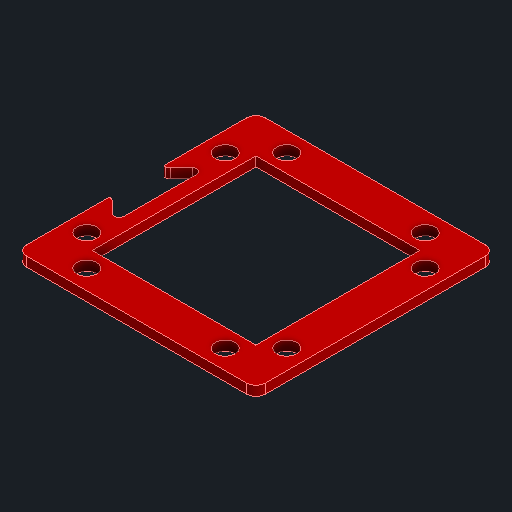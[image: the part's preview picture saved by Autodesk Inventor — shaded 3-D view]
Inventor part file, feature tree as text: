
AUTODESK INVENTOR PART (.ipt)
format: ipt  version: 2023.4 (Build 274418000, 418)  size: 366,080 bytes
history: native  units: mm
features: reference x9, extrude x3, other x3, sketch x2, fillet x1, projected_geometry x1
ambient origin geometry x8: Origin, YZ Plane, XZ Plane, XY Plane, X Axis, Y Axis, Z Axis, Center Point
bodies: Solid1 (feature_tree)
feature tree (19):
  extrude  "Extrusion1"  Depth=2.0mm TaperAngle=0.0deg
  sketch  "Sketch2"  dims[d16=10.0mm d17=0.0mm d18=0.25mm d19=20.0mm d20=10.0mm d21=45.0deg d22=1.0mm d23=1.5mm d24=1.0mm d25=0.075mm d28=15.171573mm d29=2.87868mm d30=2.87868mm d31=20.0mm d32=10.0mm d33=45.0deg d34=1.0mm d35=1.5mm d36=1.0mm d37=0.075mm d38=15.171573mm d39=2.87868mm d40=2.87868mm d41=0.25mm d42=0.0mm d43=40.0mm d45=360.0deg]
  extrude  "Extrusion2"  Depth=0.25mm
  extrude  "Extrusion3"  Depth=0.25mm
  fillet  "Fillet1"  Radius=2.87868mm
  sketch  "Sketch1"  dims[d0=2.0mm d1=0.0mm d14=2.0mm d15=0.0mm]
  reference  "Reference1"
  reference  "Reference2"
  reference  "Reference3"
  reference  "Reference4"
  reference  "Reference5"
  reference  "Reference6"
  reference  "Reference7"
  reference  "Reference8"
  reference  "Reference9"
  projected_geometry  "Projected Loop2"
  other  "<path>\Projects\Project Protocube\Protocube\CAD, STL, OBJ Files\1 CAD\Cube 1x1 V5.iam"
  other  "Cube 1x1 V5.iam"
  other  "Cube 1x1 Top V5:1"
note: 1 file-system path scrubbed to <path> (originals preserved in map.json)
